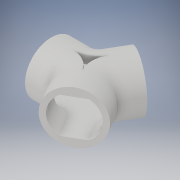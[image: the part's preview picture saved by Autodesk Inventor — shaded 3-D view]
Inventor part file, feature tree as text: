
AUTODESK INVENTOR PART (.ipt)
format: ipt  version: 2017 (Build 210142000, 142)  size: 244,224 bytes
history: native  units: in
note: dims shown in document units (in); Inventor stores cm internally (conversion verified against a paired STEP export)
features: sketch x4, extrude x2, other x2, pattern_circular x2, sweep x1
ambient origin geometry x8: Origin, YZ Plane, XZ Plane, XY Plane, X Axis, Y Axis, Z Axis, Center Point
bodies: Solid1 (feature_tree)
feature tree (11):
  extrude  "corridor"  Depth=6.6667in TaperAngle=0.0deg
  other  "found rotaion axis"
  other  "rotaion axis"
  pattern_circular  "other corridors"  Count=3 Angle=360.0deg
  sweep  "curve edjes"
  pattern_circular  "repeat curve edjes"  [2 undecoded]
  extrude  "Extrusion2"  [1 undecoded]
  sketch  "Sketch1"  dims[d10=6.6667in d11=4.0in d12=4.0in d13=0.0in]
  sketch  "Sketch4"  dims[d14=9.7746in]
  sketch  "Sketch5"  dims[d15=2.8217in d16=1.1811in d17=360.0deg]
  sketch  "Sketch7"  dims[d24=0.0in d25=0.0in d26=1.1811in d27=360.0deg d37=1.554in d38=0.0in]
note: 3 required parameter values undecoded (feature->parameter linkage not recoverable at this tier; creation-order binding heuristic only, values carry confidence <= 0.55)
